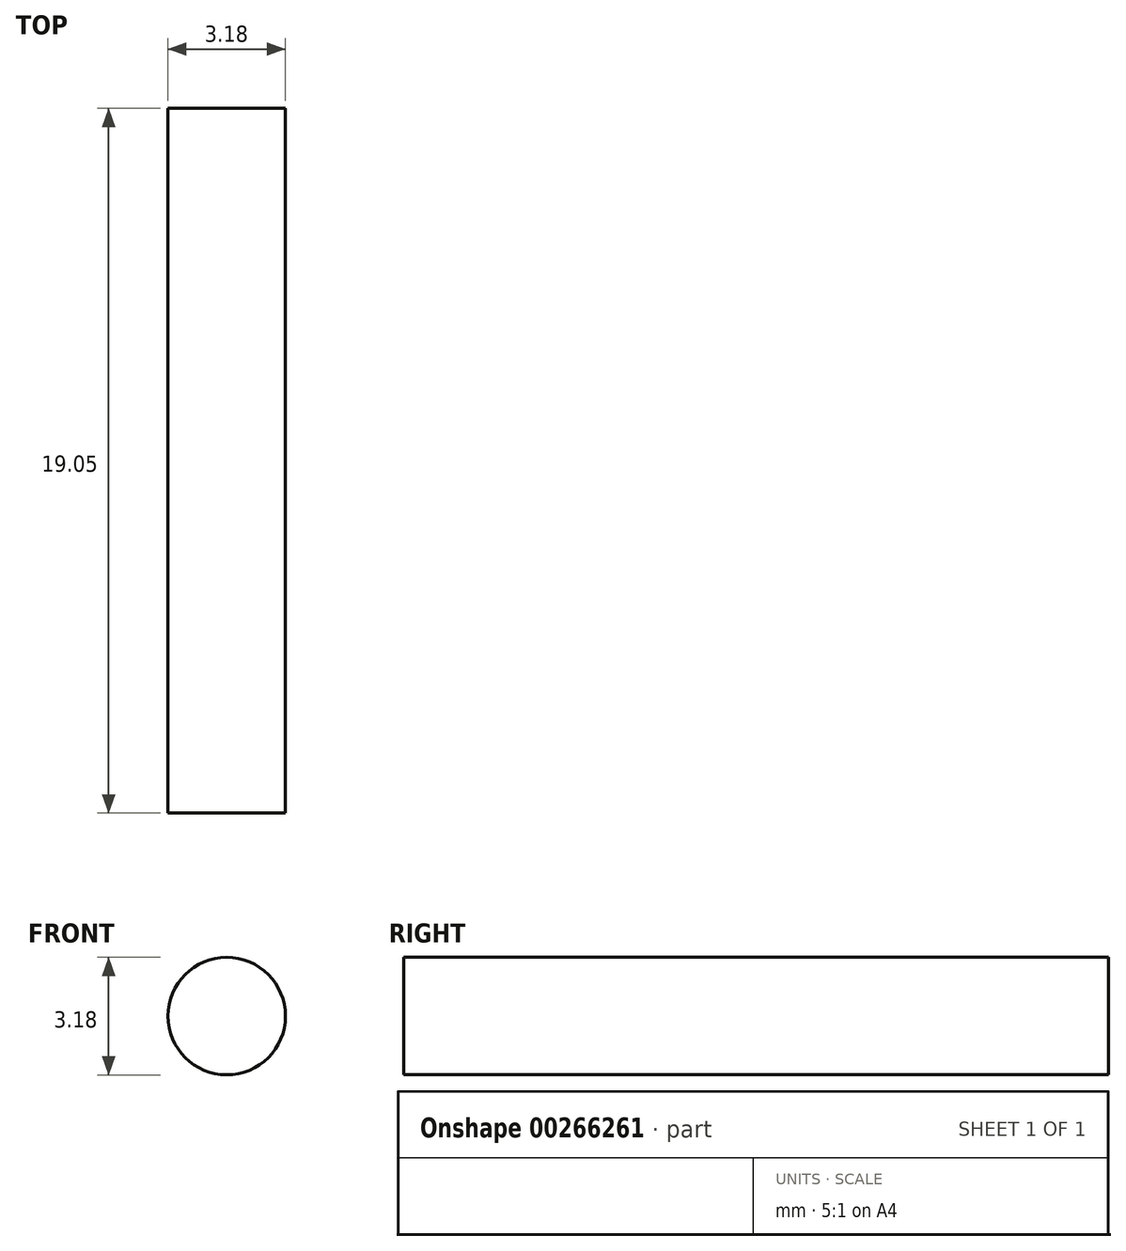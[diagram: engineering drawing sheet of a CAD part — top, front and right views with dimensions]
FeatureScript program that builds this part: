
annotation { "Feature Type Name" : "Feature", "Feature Type Description" : "" }
export const myFeature = defineFeature(function(context is Context, id is Id, definition is map)
    precondition{}
    {
        {
            var Q0;
            Q0=qCreatedBy(makeId("Front.planeOp"),FACE);
            var sketch = newSketch(context, id + "F0", { "sketchPlane" : qUnion([Q0])});
            skCircle(sketch, "E0", {"center": v(0, 0) * mm, "radius": 1.59 * mm});
            skSolve(sketch);
        }
        {
            var Q0;
            Q0=qSketchRegion(id+"F0",true);
            extrude(context, id + "F1", {"entities" : qUnion([Q0]), "depth" : 19.05 * mm});
        }
    });
